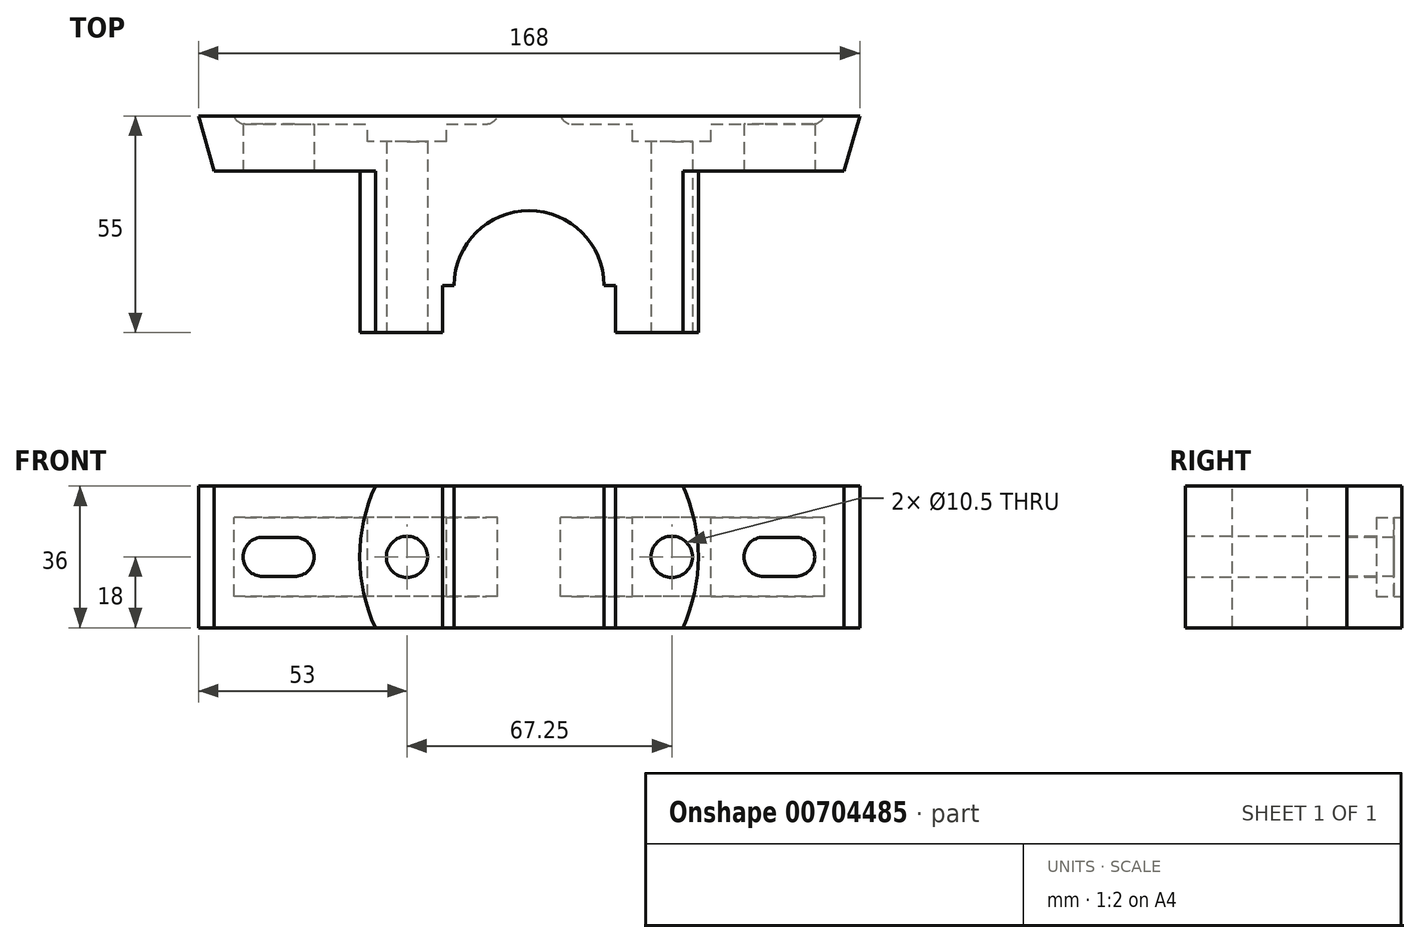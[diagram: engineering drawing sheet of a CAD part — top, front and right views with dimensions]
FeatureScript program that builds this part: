
annotation { "Feature Type Name" : "Feature", "Feature Type Description" : "" }
export const myFeature = defineFeature(function(context is Context, id is Id, definition is map)
    precondition{}
    {
        {
            var Q0;
            Q0=qCreatedBy(makeId("Front.planeOp"),FACE);
            var sketch = newSketch(context, id + "F0", { "sketchPlane" : qUnion([Q0])});
            skLineSegment(sketch, "E0.bottom", {"start": v(84, 18) * mm, "end": v(-84, 18) * mm});
            skLineSegment(sketch, "E0.top", {"start": v(84, -18) * mm, "end": v(-84, -18) * mm});
            skLineSegment(sketch, "E0.left", {"start": v(84, 18) * mm, "end": v(84, -18) * mm});
            skLineSegment(sketch, "E0.right", {"start": v(-84, 18) * mm, "end": v(-84, -18) * mm});
            skPoint(sketch, "E0.middle", {"position": v(0, 0) * mm});
            skSolve(sketch);
        }
        {
            var Q0;
            Q0=qSketchRegion(id+"F0",true);
            extrude(context, id + "F1", {"entities" : qUnion([Q0]), "depth" : 14 * mm, "offsetDistance" : 25 * mm});
        }
        {
            var Q0;
            Q0=makeQuery(id+"F1.opExtrude","SWEPT_FACE",FACE,{"disambiguationData":[OSD([sQuery(id+"F0.wireOp",EDGE,"E0.top")])]});
            var sketch = newSketch(context, id + "F2", { "sketchPlane" : qUnion([Q0])});
            skLineSegment(sketch, "E1", {"start": v(-84, 0) * mm, "end": v(-84, 14) * mm});
            skLineSegment(sketch, "E2", {"start": v(-84, 14) * mm, "end": v(-80, 14) * mm});
            skLineSegment(sketch, "E3", {"start": v(-80, 14) * mm, "end": v(-84, 0) * mm});
            skLineSegment(sketch, "E4", {"start": v(84, 0) * mm, "end": v(80, 14) * mm});
            skLineSegment(sketch, "E5", {"start": v(80, 14) * mm, "end": v(84, 14) * mm});
            skLineSegment(sketch, "E6", {"start": v(84, 14) * mm, "end": v(84, 0) * mm});
            skSolve(sketch);
        }
        {
            var Q0;
            Q0=qSketchRegion(id+"F2",true);
            extrude(context, id + "F3", {"entities" : qUnion([Q0]), "operationType" : NewBodyOperationType.REMOVE, "endBound" : BoundingType.THROUGH_ALL, "oppositeDirection" : true, "depth" : 25 * mm, "offsetDistance" : 25 * mm});
        }
        {
            var Q0;
            Q0=makeQuery(id+"F1.opExtrude","CAP_FACE",FACE,{"disambiguationData":[OSD([sQuery(id+"F0.wireOp",EDGE,"E0.bottom"),sQuery(id+"F0.wireOp",EDGE,"E0.top"),sQuery(id+"F0.wireOp",EDGE,"E0.left"),sQuery(id+"F0.wireOp",EDGE,"E0.right")])],"isStart":false});
            var sketch = newSketch(context, id + "F4", { "sketchPlane" : qUnion([Q0])});
            skLineSegment(sketch, "E7.bottom", {"start": v(39.05, 18) * mm, "end": v(-39.05, 18) * mm});
            skLineSegment(sketch, "E7.top", {"start": v(39.05, -18) * mm, "end": v(-39.05, -18) * mm});
            skPoint(sketch, "E7.middle", {"position": v(0, 0) * mm});
            skArc(sketch, "E8", {"start": v(-39.05, 18) * mm, "mid": v(-43, 0) * mm, "end": v(-39.05, -18) * mm});
            skArc(sketch, "E9.trimOffspring", {"start": v(39.05, -18) * mm, "mid": v(43, 0) * mm, "end": v(39.05, 18) * mm});
            skPoint(sketch, "E10.orphan", {"position": v(-43, 18) * mm});
            skPoint(sketch, "E7.right.end.orphan", {"position": v(-43, -18) * mm});
            skPoint(sketch, "E11.orphan", {"position": v(43, 18) * mm});
            skPoint(sketch, "E7.left.end.orphan", {"position": v(43, -18) * mm});
            skSolve(sketch);
        }
        {
            var Q0;
            Q0=qSketchRegion(id+"F4",true);
            extrude(context, id + "F5", {"entities" : qUnion([Q0]), "operationType" : NewBodyOperationType.ADD, "depth" : 41 * mm, "offsetDistance" : 25 * mm});
        }
        {
            var Q0;
            Q0=makeQuery(id+"F5.opExtrude","CAP_FACE",FACE,{"disambiguationData":[OSD([sQuery(id+"F4.wireOp",EDGE,"E7.bottom"),sQuery(id+"F4.wireOp",EDGE,"E7.top"),sQuery(id+"F4.wireOp",EDGE,"E8"),sQuery(id+"F4.wireOp",EDGE,"E9.trimOffspring")])],"isStart":false});
            var sketch = newSketch(context, id + "F6", { "sketchPlane" : qUnion([Q0])});
            skCircle(sketch, "E12", {"center": v(36.25, 0) * mm, "radius": 5.25 * mm});
            skPoint(sketch, "E12.centerSnap0", {"position": v(43, 0) * mm});
            skCircle(sketch, "E13", {"center": v(-31, 0) * mm, "radius": 5.25 * mm});
            skPoint(sketch, "E14.endSnap0", {"position": v(0, -18) * mm});
            skLineSegment(sketch, "E15", {"start": v(0, 18) * mm, "end": v(0, 25.48) * mm, "construction": true});
            skSolve(sketch);
        }
        {
            var Q0;
            Q0=qSketchRegion(id+"F6",true);
            extrude(context, id + "F7", {"entities" : qUnion([Q0]), "operationType" : NewBodyOperationType.REMOVE, "endBound" : BoundingType.THROUGH_ALL, "oppositeDirection" : true, "depth" : 25 * mm, "offsetDistance" : 25 * mm});
        }
        {
            var Q0;
            Q0=makeQuery(id+"F1.opExtrude","CAP_FACE",FACE,{"disambiguationData":[OSD([sQuery(id+"F0.wireOp",EDGE,"E0.bottom"),sQuery(id+"F0.wireOp",EDGE,"E0.top"),sQuery(id+"F0.wireOp",EDGE,"E0.left"),sQuery(id+"F0.wireOp",EDGE,"E0.right")])],"isStart":true});
            var sketch = newSketch(context, id + "F8", { "sketchPlane" : qUnion([Q0])});
            skLineSegment(sketch, "E16.bottom", {"start": v(-46.25, 10) * mm, "end": v(-26.25, 10) * mm});
            skLineSegment(sketch, "E16.top", {"start": v(-46.25, -10) * mm, "end": v(-26.25, -10) * mm});
            skLineSegment(sketch, "E16.left", {"start": v(-46.25, 10) * mm, "end": v(-46.25, -10) * mm});
            skLineSegment(sketch, "E16.right", {"start": v(-26.25, 10) * mm, "end": v(-26.25, -10) * mm});
            skPoint(sketch, "E16.middle", {"position": v(-36.25, 0) * mm});
            skLineSegment(sketch, "E17.bottom", {"start": v(21, 10) * mm, "end": v(41, 10) * mm});
            skLineSegment(sketch, "E17.top", {"start": v(21, -10) * mm, "end": v(41, -10) * mm});
            skLineSegment(sketch, "E17.left", {"start": v(21, 10) * mm, "end": v(21, -10) * mm});
            skLineSegment(sketch, "E17.right", {"start": v(41, 10) * mm, "end": v(41, -10) * mm});
            skPoint(sketch, "E17.middle", {"position": v(31, 0) * mm});
            skSolve(sketch);
        }
        {
            var Q0;
            Q0=qSketchRegion(id+"F8",true);
            extrude(context, id + "F9", {"entities" : qUnion([Q0]), "operationType" : NewBodyOperationType.REMOVE, "oppositeDirection" : true, "depth" : 6.5 * mm, "offsetDistance" : 25 * mm});
        }
        {
            var Q0;
            Q0=makeQuery(id+"F1.opExtrude","CAP_FACE",FACE,{"disambiguationData":[OSD([sQuery(id+"F0.wireOp",EDGE,"E0.bottom"),sQuery(id+"F0.wireOp",EDGE,"E0.top"),sQuery(id+"F0.wireOp",EDGE,"E0.left"),sQuery(id+"F0.wireOp",EDGE,"E0.right")])],"isStart":true});
            var sketch = newSketch(context, id + "F10", { "sketchPlane" : qUnion([Q0])});
            skLineSegment(sketch, "E18.bottom", {"start": v(75, -10) * mm, "end": v(8, -10) * mm});
            skLineSegment(sketch, "E18.top", {"start": v(75, 10) * mm, "end": v(8, 10) * mm});
            skLineSegment(sketch, "E18.left", {"start": v(75, -10) * mm, "end": v(75, 10) * mm});
            skLineSegment(sketch, "E18.right", {"start": v(8, -10) * mm, "end": v(8, 10) * mm});
            skLineSegment(sketch, "E19.bottom", {"start": v(-8, -10) * mm, "end": v(-75, -10) * mm});
            skLineSegment(sketch, "E19.top", {"start": v(-8, 10) * mm, "end": v(-75, 10) * mm});
            skLineSegment(sketch, "E19.left", {"start": v(-8, -10) * mm, "end": v(-8, 10) * mm});
            skLineSegment(sketch, "E19.right", {"start": v(-75, -10) * mm, "end": v(-75, 10) * mm});
            skSolve(sketch);
        }
        {
            var Q0;
            Q0=qSketchRegion(id+"F10",true);
            extrude(context, id + "F11", {"entities" : qUnion([Q0]), "operationType" : NewBodyOperationType.REMOVE, "oppositeDirection" : true, "depth" : 2 * mm, "offsetDistance" : 25 * mm});
        }
        {
            var Q0;
            Q0=makeQuery(id+"F11.boolean.opBoolean","COPY",EDGE,{"derivedFrom":makeQuery(id+"F11.opExtrude","CAP_EDGE",EDGE,{"disambiguationData":[OSD([sQuery(id+"F10.wireOp",EDGE,"E19.right")])],"isStart":false})});
            var Q1;
            Q1=makeQuery(id+"F11.boolean.opBoolean","COPY",EDGE,{"derivedFrom":makeQuery(id+"F11.opExtrude","CAP_EDGE",EDGE,{"disambiguationData":[OSD([sQuery(id+"F10.wireOp",EDGE,"E19.left")])],"isStart":false})});
            var Q2;
            Q2=makeQuery(id+"F11.boolean.opBoolean","COPY",EDGE,{"derivedFrom":makeQuery(id+"F11.opExtrude","CAP_EDGE",EDGE,{"disambiguationData":[OSD([sQuery(id+"F10.wireOp",EDGE,"E18.left")])],"isStart":false})});
            var Q3;
            Q3=makeQuery(id+"F11.boolean.opBoolean","COPY",EDGE,{"derivedFrom":makeQuery(id+"F11.opExtrude","CAP_EDGE",EDGE,{"disambiguationData":[OSD([sQuery(id+"F10.wireOp",EDGE,"E18.right")])],"isStart":false})});
            fillet(context, id + "F12", {"entities" : qUnion([Q0, Q1, Q2, Q3]), "radius" : 3 * mm, "tangentPropagation" : true, "allowEdgeOverflow" : false});
        }
        {
            var Q0;
            {var subQ0=sQuery(id+"F0.wireOp",EDGE,"E0.top");var subQ1=sQuery(id+"F0.wireOp",EDGE,"E0.bottom");Q0=makeQuery(id+"F5.boolean.opBoolean","SPLIT",FACE,{"disambiguationData":[TD([makeQuery(id+"F3.boolean.opBoolean","COPY",FACE,{"derivedFrom":makeQuery(id+"F3.opExtrude","SWEPT_FACE",FACE,{"disambiguationData":[OSD([sQuery(id+"F2.wireOp",EDGE,"E4")])]})})])],"derivedFrom":makeQuery(id+"F1.opExtrude","CAP_FACE",FACE,{"disambiguationData":[OSD([subQ1,subQ0,sQuery(id+"F0.wireOp",EDGE,"E0.left"),sQuery(id+"F0.wireOp",EDGE,"E0.right")])],"isStart":false})});}
            var sketch = newSketch(context, id + "F13", { "sketchPlane" : qUnion([Q0])});
            skLineSegment(sketch, "E20.bottom", {"start": v(59.58, -5) * mm, "end": v(67.58, -5) * mm});
            skLineSegment(sketch, "E20.top", {"start": v(59.58, 5) * mm, "end": v(67.58, 5) * mm});
            skLineSegment(sketch, "E20.left", {"start": v(54.58, 0) * mm, "end": v(54.58, 0) * mm});
            skLineSegment(sketch, "E20.right", {"start": v(72.58, 0) * mm, "end": v(72.58, 0) * mm});
            skPoint(sketch, "E20.middle", {"position": v(63.58, 0) * mm});
            skLineSegment(sketch, "E21.bottom", {"start": v(-67.64, -5) * mm, "end": v(-59.64, -5) * mm});
            skLineSegment(sketch, "E21.top", {"start": v(-67.64, 5) * mm, "end": v(-59.64, 5) * mm});
            skPoint(sketch, "E21.middle", {"position": v(-63, 0) * mm});
            skPoint(sketch, "E22.visualSharp", {"position": v(72.58, -5) * mm});
            skArc(sketch, "E22.filletArc", {"start": v(67.58, -5) * mm, "mid": v(71.11, -3.54) * mm, "end": v(72.58, 0) * mm});
            skPoint(sketch, "E23.visualSharp", {"position": v(72.58, 5) * mm});
            skArc(sketch, "E23.filletArc", {"start": v(72.58, 0) * mm, "mid": v(71.11, 3.54) * mm, "end": v(67.58, 5) * mm});
            skPoint(sketch, "E24.visualSharp", {"position": v(54.58, 5) * mm});
            skArc(sketch, "E24.filletArc", {"start": v(59.58, 5) * mm, "mid": v(56.04, 3.54) * mm, "end": v(54.58, 0) * mm});
            skPoint(sketch, "E25.visualSharp", {"position": v(54.58, -5) * mm});
            skArc(sketch, "E25.filletArc", {"start": v(54.58, 0) * mm, "mid": v(56.04, -3.54) * mm, "end": v(59.58, -5) * mm});
            skArc(sketch, "E26", {"start": v(-59.64, -5) * mm, "mid": v(-54.64, 0) * mm, "end": v(-59.64, 5) * mm});
            skArc(sketch, "E27", {"start": v(-67.64, 5) * mm, "mid": v(-72.64, 0) * mm, "end": v(-67.64, -5) * mm});
            skPoint(sketch, "E28.orphan", {"position": v(-55.1, -5) * mm});
            skPoint(sketch, "E29.orphan", {"position": v(-70.92, 5) * mm});
            skPoint(sketch, "E30.orphan", {"position": v(-70.89, -5) * mm});
            skSolve(sketch);
        }
        {
            var Q0;
            Q0=makeQuery(id+"F13.imprint","IMPRINT",FACE,{"disambiguationData":[TD([[makeQuery(id+"F13.imprint","IMPRINT",EDGE,{"derivedFrom":sQuery(id+"F13.wireOp",EDGE,"E21.bottom")}),1.0]])]});
            var Q1;
            Q1=makeQuery(id+"F13.imprint","IMPRINT",FACE,{"disambiguationData":[TD([[makeQuery(id+"F13.imprint","IMPRINT",EDGE,{"derivedFrom":sQuery(id+"F13.wireOp",EDGE,"E20.bottom")}),1.0]])]});
            extrude(context, id + "F14", {"entities" : qUnion([Q0, Q1]), "operationType" : NewBodyOperationType.REMOVE, "oppositeDirection" : true, "depth" : 25 * mm, "offsetDistance" : 25 * mm});
        }
        {
            var Q0;
            Q0=makeQuery(id+"F5.boolean.opBoolean","MERGE",FACE,{"derivedFrom":[makeQuery(id+"F1.opExtrude","SWEPT_FACE",FACE,{"disambiguationData":[OSD([sQuery(id+"F0.wireOp",EDGE,"E0.bottom")])]}),makeQuery(id+"F5.opExtrude","SWEPT_FACE",FACE,{"disambiguationData":[OSD([sQuery(id+"F4.wireOp",EDGE,"E7.bottom")])]})]});
            var sketch = newSketch(context, id + "F15", { "sketchPlane" : qUnion([Q0])});
            skArc(sketch, "E31", {"start": v(19, -43) * mm, "mid": v(0, -24) * mm, "end": v(-19, -43) * mm});
            skLineSegment(sketch, "E32", {"start": v(0, -55) * mm, "end": v(22, -55) * mm});
            skLineSegment(sketch, "E33", {"start": v(22, -55) * mm, "end": v(22, -43) * mm});
            skLineSegment(sketch, "E34", {"start": v(22, -43) * mm, "end": v(19, -43) * mm});
            skLineSegment(sketch, "E35", {"start": v(0, -55) * mm, "end": v(-22, -55) * mm});
            skLineSegment(sketch, "E36", {"start": v(-22, -55) * mm, "end": v(-22, -43) * mm});
            skLineSegment(sketch, "E37", {"start": v(-22, -43) * mm, "end": v(-19, -43) * mm});
            skSolve(sketch);
        }
        {
            var Q0;
            Q0=qSketchRegion(id+"F15",true);
            extrude(context, id + "F16", {"entities" : qUnion([Q0]), "operationType" : NewBodyOperationType.REMOVE, "endBound" : BoundingType.THROUGH_ALL, "oppositeDirection" : true, "depth" : 25 * mm, "offsetDistance" : 25 * mm});
        }
    });
